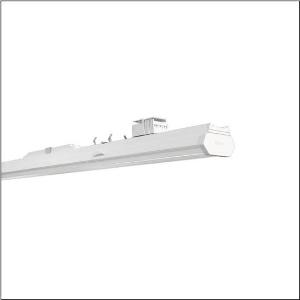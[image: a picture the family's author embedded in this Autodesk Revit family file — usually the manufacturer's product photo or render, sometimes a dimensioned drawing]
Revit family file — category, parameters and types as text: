
# Revit family: licross_r__11_protected_extreme_ho_51td1bdn4e5me_a1af
name_source: partatom
category: Lighting Fixtures
units: mm (PartAtom-declared; Revit-internal decimal feet)

## family parameters
Cut with Voids When Loaded = No
Host = Face
Light Source = No
Part Type = Normal
Room Calculation Point = No
Round Connector Dimension = Use Diameter
Shared = No

## types (1)
- --- (1 x LED, 14500 lm, 87.3 W, 4000K)
    Apparent Load = 87 VA
    CIE Flux Codes = 54 82 95 97 100
    Color Rendering = 80
    Color Temperature = 4000K
    Default Elevation = 1800 mm
    Description = Licross® 11 Protected extreme HO, luminaire insert, of sheet steel, galvanised, coil coated, white, length: 1.500mm, width: 90mm, height: 101mm, LED rated luminous flux: 14.500lm, light colour: 840, control gear: DALI 2, with plug, 5-pole, with phase selection, mains connection: 220..240V, AC, 50/60Hz, rated input power: 87W, halogen-free wiring, primary optical cover: cover, of PMMA, light emission: direct distribution, primary light characteristic: symmetric, protection rating (complete): IP54, insulation class (complete): insulation class I (protective earthing), certification: CE, ENEC, VDE, UKCA, protection symbol: D if used in an environment with non-conductive dust loads with corresponding accessories, impact resistance: IK06, permissible ambient temperature for indoor applications: -40..+40°C, corresponds to IFS (International Featured Standards) requirements for safety and quality in the food industry, reducing of maximum allowable ambient temperature of 5°C with ceiling mounting, LABS conformity tested according to VDMA 24364:2018-05, packaging unit: 1 piece
    Height = 92 mm
    Lamp = 1 x LED
    Lamp Light Flux = 14500 lm
    Lamp Power = 87.3 W
    Lamp count = 1
    Length = 1500 mm
    Luminous efficacy = 166 lm/W
    Manufacturer = Siteco
    ModVariant = No
    Model = 51TD1BDN4E5ME
    Mounting Place = Ceiling
    Mounting Type = Pendant
    Number of Poles = 1
    OnlyDefault = Yes
    Power Factor = 1
    Product Name = Licross® 11 Protected extreme HO
    Product group = luminaire insert
    ProductGroupID = 901
    Protection Class = Protection class I
    Protection Degree = IP 54
    RLX_Detail_Level = 1
    RLX_Emergency_Light_Flux = 0 lm
    RLX_Emergency_Type = 0
    RLX_Emergency_Type_DB = No
    RlxData = <blob elided: 24369 chars, md5=cd075e32>
    Socket = socket
    Standby Power = 0 W
    System Light Flux = 14500 lm
    System Power = 87 W
    Type Comments = factory setting: luminous flux: 100 % | dim-lin: 254 | 589 mA
    Type Image = l_1256145.jpg
    URL = http://relux.com
    VarID = @adj_052269
    Voltage = 0 V
    Weight = 0.00 kg
    Width = 88 mm

## geometry (parser evidence)
native form markers: Blend x4, Sweep x10
no freeform markers — native parametric forms only
